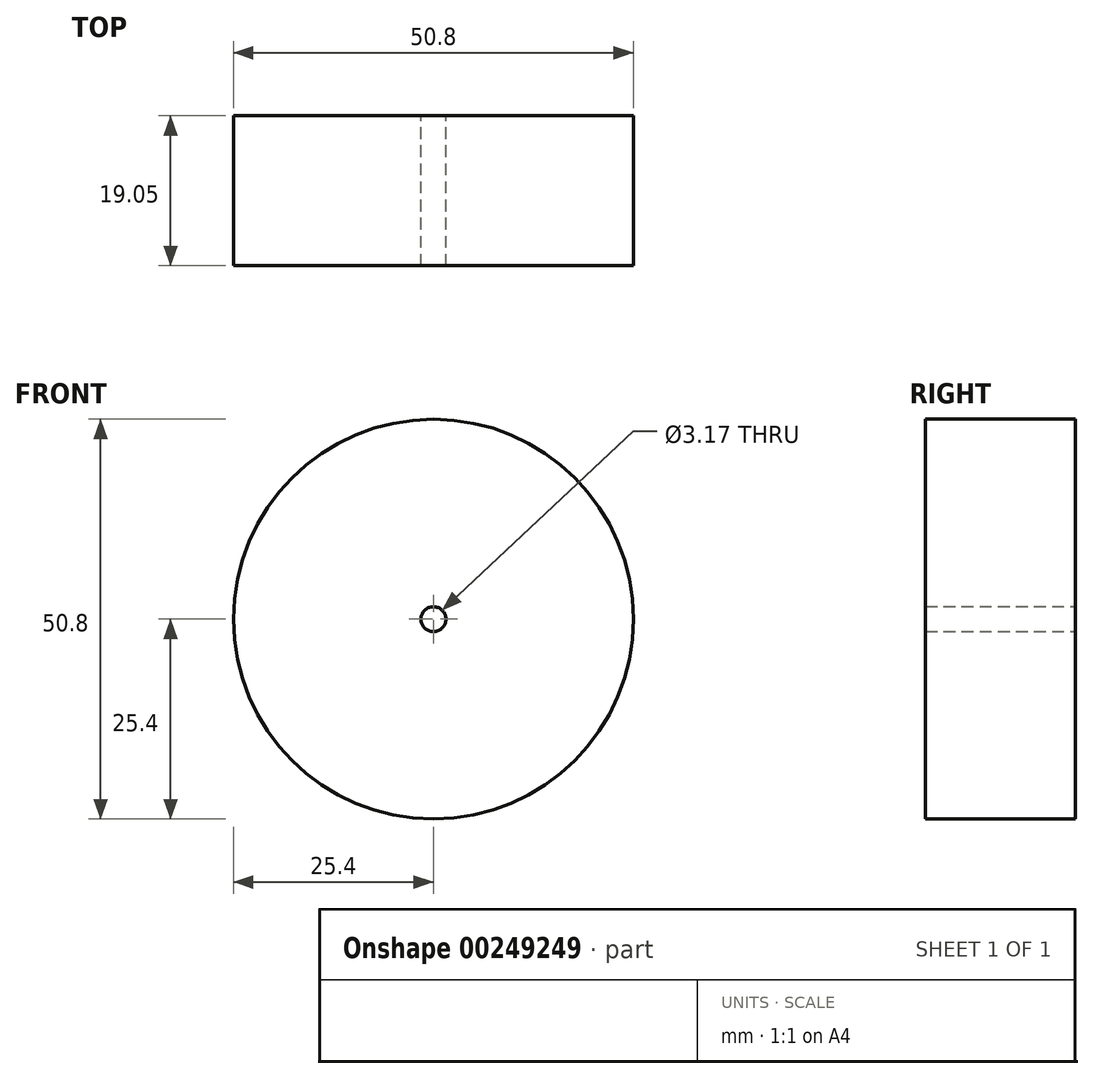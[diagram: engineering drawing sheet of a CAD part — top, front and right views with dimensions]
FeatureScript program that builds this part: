
annotation { "Feature Type Name" : "Feature", "Feature Type Description" : "" }
export const myFeature = defineFeature(function(context is Context, id is Id, definition is map)
    precondition{}
    {
        {
            var Q0;
            Q0=qCreatedBy(makeId("Front.planeOp"),FACE);
            var sketch = newSketch(context, id + "F0", { "sketchPlane" : qUnion([Q0])});
            skCircle(sketch, "E0", {"center": v(0, 0) * mm, "radius": 25.4 * mm});
            skCircle(sketch, "E1", {"center": v(0, 0) * mm, "radius": 1.59 * mm});
            skSolve(sketch);
        }
        {
            var Q0;
            Q0=makeQuery(id+"F0.imprint","IMPRINT",FACE,{"disambiguationData":[TD([[makeQuery(id+"F0.imprint","IMPRINT",EDGE,{"derivedFrom":sQuery(id+"F0.wireOp",EDGE,"E0")}),1.0]])]});
            extrude(context, id + "F1", {"entities" : qUnion([Q0]), "depth" : 19.05 * mm});
        }
    });
